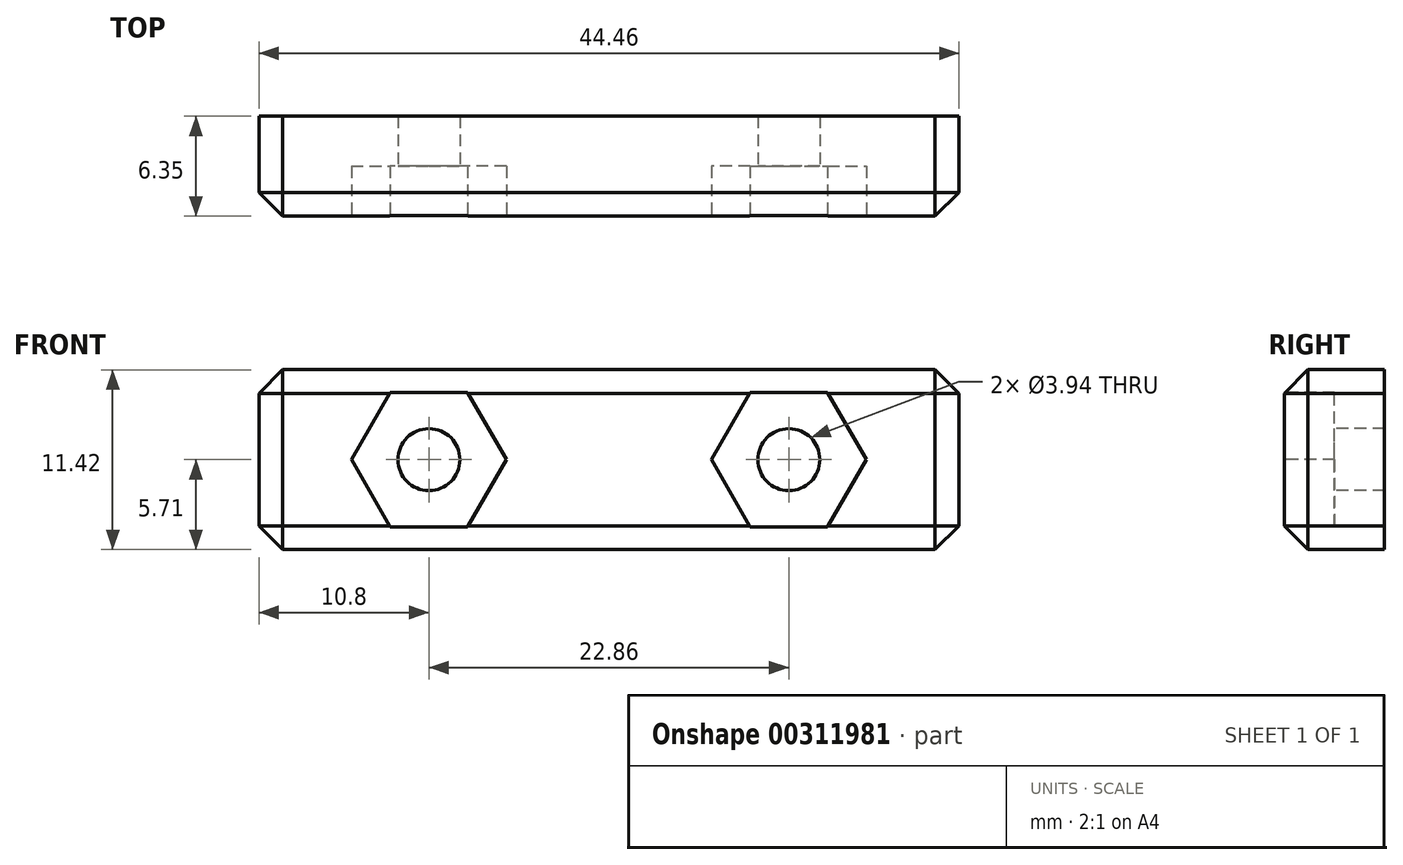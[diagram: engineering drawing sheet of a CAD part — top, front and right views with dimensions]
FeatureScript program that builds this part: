
annotation { "Feature Type Name" : "Feature", "Feature Type Description" : "" }
export const myFeature = defineFeature(function(context is Context, id is Id, definition is map)
    precondition{}
    {
        {
            var Q0;
            Q0=qCreatedBy(makeId("Front.planeOp"),FACE);
            var sketch = newSketch(context, id + "F0", { "sketchPlane" : qUnion([Q0])});
            skLineSegment(sketch, "E0.bottom", {"start": v(-22.23, 5.71) * mm, "end": v(22.23, 5.71) * mm});
            skLineSegment(sketch, "E0.top", {"start": v(-22.23, -5.71) * mm, "end": v(22.23, -5.71) * mm});
            skLineSegment(sketch, "E0.left", {"start": v(-22.23, 5.71) * mm, "end": v(-22.23, -5.71) * mm});
            skLineSegment(sketch, "E0.right", {"start": v(22.23, 5.71) * mm, "end": v(22.23, -5.71) * mm});
            skPoint(sketch, "E0.middle", {"position": v(0, 0) * mm});
            skPoint(sketch, "E1", {"position": v(-11.43, 0) * mm});
            skPoint(sketch, "E2", {"position": v(11.43, 0) * mm});
            skSolve(sketch);
        }
        {
            var Q0;
            Q0=qSketchRegion(id+"F0",true);
            extrude(context, id + "F1", {"entities" : qUnion([Q0]), "oppositeDirection" : true, "depth" : 6.35 * mm});
        }
        {
            var Q0;
            Q0=makeQuery(id+"F1.opExtrude","CAP_FACE",FACE,{"disambiguationData":[OSD([sQuery(id+"F0.wireOp",EDGE,"E0.bottom"),sQuery(id+"F0.wireOp",EDGE,"E0.top"),sQuery(id+"F0.wireOp",EDGE,"E0.left"),sQuery(id+"F0.wireOp",EDGE,"E0.right")])],"isStart":true});
            var sketch = newSketch(context, id + "F2", { "sketchPlane" : qUnion([Q0])});
            skCircle(sketch, "E3.cCircle", {"center": v(-11.43, 0) * mm, "radius": 4.26 * mm, "construction": true});
            skLineSegment(sketch, "E3.0", {"start": v(-8.97, -4.26) * mm, "end": v(-13.9, -4.26) * mm});
            skLineSegment(sketch, "E3.1", {"start": v(-13.9, -4.26) * mm, "end": v(-16.35, 0) * mm});
            skLineSegment(sketch, "E3.2", {"start": v(-16.35, 0) * mm, "end": v(-13.9, 4.26) * mm});
            skLineSegment(sketch, "E3.3", {"start": v(-13.9, 4.26) * mm, "end": v(-8.97, 4.26) * mm});
            skLineSegment(sketch, "E3.4", {"start": v(-8.97, 4.26) * mm, "end": v(-6.5, 0) * mm});
            skLineSegment(sketch, "E3.5", {"start": v(-6.5, 0) * mm, "end": v(-8.97, -4.26) * mm});
            skPoint(sketch, "E3.0.midPoint", {"position": v(-11.43, -4.26) * mm});
            skPoint(sketch, "E4.MirrorP", {"position": v(11.43, -4.26) * mm});
            skCircle(sketch, "E5.MirrorC", {"center": v(11.43, 0) * mm, "radius": 4.26 * mm, "construction": true});
            skLineSegment(sketch, "E6.MirrorCS", {"start": v(8.97, -4.26) * mm, "end": v(13.9, -4.26) * mm});
            skLineSegment(sketch, "E7.MirrorCS", {"start": v(16.35, 0) * mm, "end": v(13.9, 4.26) * mm});
            skLineSegment(sketch, "E8.MirrorCS", {"start": v(6.5, 0) * mm, "end": v(8.97, -4.26) * mm});
            skLineSegment(sketch, "E9.MirrorCS", {"start": v(13.9, 4.26) * mm, "end": v(8.97, 4.26) * mm});
            skLineSegment(sketch, "E10.MirrorCS", {"start": v(13.9, -4.26) * mm, "end": v(16.35, 0) * mm});
            skLineSegment(sketch, "E11.MirrorCS", {"start": v(8.97, 4.26) * mm, "end": v(6.5, 0) * mm});
            skSolve(sketch);
        }
        {
            var Q0;
            Q0=makeQuery(id+"F1.opExtrude","CAP_EDGE",EDGE,{"disambiguationData":[OSD([sQuery(id+"F0.wireOp",EDGE,"E0.bottom")])],"isStart":true});
            var Q1;
            Q1=makeQuery(id+"F1.opExtrude","CAP_EDGE",EDGE,{"disambiguationData":[OSD([sQuery(id+"F0.wireOp",EDGE,"E0.top")])],"isStart":true});
            var Q2;
            Q2=makeQuery(id+"F1.opExtrude","CAP_EDGE",EDGE,{"disambiguationData":[OSD([sQuery(id+"F0.wireOp",EDGE,"E0.right")])],"isStart":true});
            var Q3;
            Q3=makeQuery(id+"F1.opExtrude","CAP_EDGE",EDGE,{"disambiguationData":[OSD([sQuery(id+"F0.wireOp",EDGE,"E0.left")])],"isStart":true});
            var Q4;
            Q4=makeQuery(id+"F1.opExtrude","SWEPT_EDGE",EDGE,{"disambiguationData":[OSD([sQuery(id+"F0.wireOp",EDGE,"E0.top"),sQuery(id+"F0.wireOp",EDGE,"E0.right")])]});
            var Q5;
            Q5=makeQuery(id+"F1.opExtrude","SWEPT_EDGE",EDGE,{"disambiguationData":[OSD([sQuery(id+"F0.wireOp",EDGE,"E0.bottom"),sQuery(id+"F0.wireOp",EDGE,"E0.right")])]});
            var Q6;
            Q6=makeQuery(id+"F1.opExtrude","SWEPT_EDGE",EDGE,{"disambiguationData":[OSD([sQuery(id+"F0.wireOp",EDGE,"E0.bottom"),sQuery(id+"F0.wireOp",EDGE,"E0.left")])]});
            var Q7;
            Q7=makeQuery(id+"F1.opExtrude","SWEPT_EDGE",EDGE,{"disambiguationData":[OSD([sQuery(id+"F0.wireOp",EDGE,"E0.top"),sQuery(id+"F0.wireOp",EDGE,"E0.left")])]});
            chamfer(context, id + "F3", {"entities" : qUnion([Q0, Q1, Q2, Q3, Q4, Q5, Q6, Q7]), "width" : 1.5 * mm, "tangentPropagation" : true});
        }
        {
            var Q0;
            Q0 = qSketchRegion(id + "F2", true);
            extrude(context, id + "F4", {"entities" : qUnion([Q0]), "operationType" : NewBodyOperationType.REMOVE, "oppositeDirection" : true, "depth" : 3.17 * mm});
        }
        {
            var Q0;
            Q0=sQuery(id+"F0.wireOp",VERTEX,"E1");
            var Q1;
            Q1=sQuery(id+"F0.wireOp",VERTEX,"E2");
            var Q2;
            Q2=makeQuery(id+"F1.opExtrude","SWEPT_BODY",BODY,{"disambiguationData":[OSD([sQuery(id+"F0.wireOp",EDGE,"E0.bottom"),sQuery(id+"F0.wireOp",EDGE,"E0.top"),sQuery(id+"F0.wireOp",EDGE,"E0.left"),sQuery(id+"F0.wireOp",EDGE,"E0.right")])]});
            hole(context, id + "F5", {"style" : HoleStyle.SIMPLE, "endStyle" : HoleEndStyle.BLIND, "holeDiameter" : 3.94 * mm, "holeDepth" : 6.35 * mm, "tappedDepth" : 12.7 * mm, "tapClearance" : 3, "locations" : qUnion([Q0, Q1]), "scope" : qUnion([Q2])});
        }
    });
